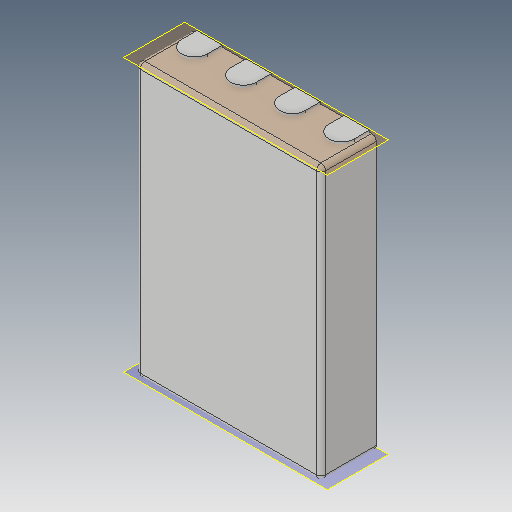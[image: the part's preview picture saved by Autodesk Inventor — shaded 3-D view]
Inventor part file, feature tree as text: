
AUTODESK INVENTOR PART (.ipt)
format: ipt  version: 2020 (Build 240168000, 168)  size: 194,560 bytes
history: native  units: mm
features: other x7, projected_geometry x5, extrude x3, sketch x3, plane x2, fillet x1
ambient origin geometry x8: Origin, YZ Plane, XZ Plane, XY Plane, X Axis, Y Axis, Z Axis, Center Point
bodies: Body1 (feature_tree), Body2 (feature_tree), Body3 (feature_tree)
feature tree (21):
  other  "Sólido1"
  extrude  "Extrusión1"  TaperAngle=90.0deg  [1 undecoded]
  plane  "Plano de trabajo1"
  extrude  "Extrusión2"  Depth=0.3mm TaperAngle=0.0deg
  plane  "Plano de trabajo2"
  extrude  "Extrusión3"  Depth=0.3mm TaperAngle=0.0deg
  fillet  "Empalme1"  Radius=0.05mm
  other  "Edición directa1"
  other  "Edición directa2"
  sketch  "Boceto1"  dims[d0=0.6mm d1=0.0mm d2=90.0deg]
  sketch  "Boceto2"  dims[d3=40.0mm d5=0.53mm d6=10.0mm d8=10.0mm d10=0.3mm d11=0.0mm]
  other  "Sólido2"
  sketch  "Boceto3"  dims[d12=90.0deg d13=0.3mm d14=0.0mm d15=0.05mm d16=0.0mm d17=0.0mm d18=0.02mm d19=0.0mm d20=0.0mm d21=0.02mm]
  projected_geometry  "Contorno proyectado1"
  projected_geometry  "Contorno proyectado2"
  projected_geometry  "Contorno proyectado3"
  projected_geometry  "Contorno proyectado4"
  projected_geometry  "Contorno proyectado5"
  other  "Sólido3"
  other  "Desplazar1"
  other  "Desplazar2"
note: 1 required parameter value undecoded (feature->parameter linkage not recoverable at this tier; creation-order binding heuristic only, values carry confidence <= 0.55)
